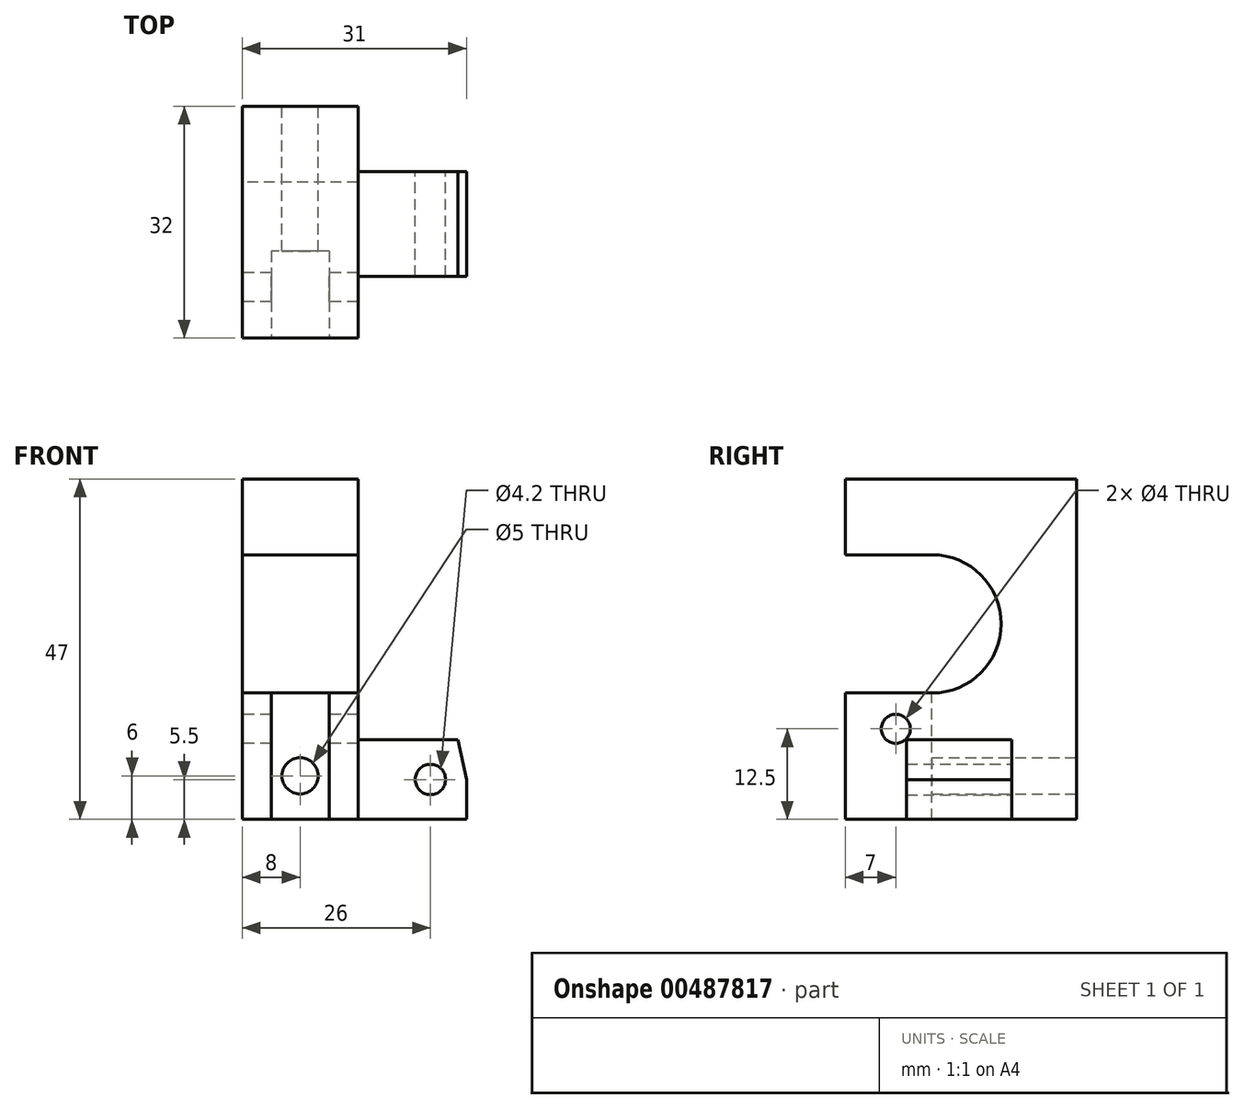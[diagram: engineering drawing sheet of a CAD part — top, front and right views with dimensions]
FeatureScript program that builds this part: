
annotation { "Feature Type Name" : "Feature", "Feature Type Description" : "" }
export const myFeature = defineFeature(function(context is Context, id is Id, definition is map)
    precondition{}
    {
        {
            var Q0;
            Q0=qCreatedBy(makeId("Right.planeOp"),FACE);
            var sketch = newSketch(context, id + "F0", { "sketchPlane" : qUnion([Q0])});
            skArc(sketch, "E0", {"start": v(0, -9.55) * mm, "mid": v(9.55, 0) * mm, "end": v(0, 9.55) * mm});
            skLineSegment(sketch, "E1.bottom", {"start": v(-12, 20) * mm, "end": v(20, 20) * mm});
            skLineSegment(sketch, "E1.top", {"start": v(-12, -27) * mm, "end": v(20, -27) * mm});
            skLineSegment(sketch, "E1.left", {"start": v(-12, 20) * mm, "end": v(-12, -27) * mm});
            skLineSegment(sketch, "E1.right", {"start": v(20, 20) * mm, "end": v(20, -27) * mm});
            skLineSegment(sketch, "E2.bottom", {"start": v(0, 9.55) * mm, "end": v(-12, 9.55) * mm});
            skLineSegment(sketch, "E2.top", {"start": v(0, -9.55) * mm, "end": v(-12, -9.55) * mm});
            skPoint(sketch, "E3.orphan", {"position": v(20, 9.55) * mm});
            skPoint(sketch, "E4.orphan", {"position": v(20, -9.55) * mm});
            skPoint(sketch, "E2.right.start.orphan", {"position": v(-20, 9.55) * mm});
            skPoint(sketch, "E5.orphan", {"position": v(-20, -9.55) * mm});
            skSolve(sketch);
        }
        {
            var Q0;
            Q0=makeQuery(id+"F0.imprint","IMPRINT",FACE,{"disambiguationData":[TD([[makeQuery(id+"F0.imprint","IMPRINT",EDGE,{"derivedFrom":sQuery(id+"F0.wireOp",EDGE,"E0")}),-1.0]])]});
            extrude(context, id + "F1", {"entities" : qUnion([Q0]), "depth" : 16 * mm, "offsetDistance" : 25 * mm});
        }
        {
            var Q0;
            Q0=makeQuery(id+"F1.opExtrude","CAP_FACE",FACE,{"disambiguationData":[OSD([sQuery(id+"F0.wireOp",EDGE,"E0"),sQuery(id+"F0.wireOp",EDGE,"E1.bottom"),sQuery(id+"F0.wireOp",EDGE,"E1.top"),sQuery(id+"F0.wireOp",EDGE,"E1.left"),sQuery(id+"F0.wireOp",EDGE,"E1.right")])],"isStart":false});
            var sketch = newSketch(context, id + "F2", { "sketchPlane" : qUnion([Q0])});
            skLineSegment(sketch, "E6.bottom", {"start": v(11, -27) * mm, "end": v(-3.5, -27) * mm});
            skLineSegment(sketch, "E6.top", {"start": v(11, -16) * mm, "end": v(-3.5, -16) * mm});
            skLineSegment(sketch, "E6.left", {"start": v(11, -27) * mm, "end": v(11, -16) * mm});
            skLineSegment(sketch, "E6.right", {"start": v(-3.5, -27) * mm, "end": v(-3.5, -16) * mm});
            skSolve(sketch);
        }
        {
            var Q0;
            Q0=makeQuery(id+"F2.imprint","IMPRINT",FACE,{"disambiguationData":[TD([[makeQuery(id+"F2.imprint","IMPRINT",EDGE,{"derivedFrom":sQuery(id+"F2.wireOp",EDGE,"E6.bottom")}),1.0]])]});
            extrude(context, id + "F3", {"entities" : qUnion([Q0]), "operationType" : NewBodyOperationType.ADD, "depth" : 15 * mm, "offsetDistance" : 25 * mm});
        }
        {
            var Q0;
            Q0=makeQuery(id+"F3.opExtrude","SWEPT_FACE",FACE,{"disambiguationData":[OSD([sQuery(id+"F2.wireOp",EDGE,"E6.right")])]});
            var sketch = newSketch(context, id + "F4", { "sketchPlane" : qUnion([Q0])});
            skLineSegment(sketch, "E7", {"start": v(31, -21.5) * mm, "end": v(31, -16) * mm});
            skLineSegment(sketch, "E8", {"start": v(31, -16) * mm, "end": v(29.83, -16) * mm});
            skLineSegment(sketch, "E9", {"start": v(29.83, -16) * mm, "end": v(31, -21.5) * mm});
            skSolve(sketch);
        }
        {
            var Q0;
            Q0=makeQuery(id+"F4.imprint","IMPRINT",FACE,{"disambiguationData":[TD([[makeQuery(id+"F4.imprint","IMPRINT",EDGE,{"derivedFrom":sQuery(id+"F4.wireOp",EDGE,"E7")}),1.0]])]});
            extrude(context, id + "F5", {"entities" : qUnion([Q0]), "operationType" : NewBodyOperationType.REMOVE, "endBound" : BoundingType.THROUGH_ALL, "oppositeDirection" : true, "depth" : 25 * mm, "offsetDistance" : 25 * mm});
        }
        {
            var Q0;
            Q0=makeQuery(id+"F3.opExtrude","SWEPT_FACE",FACE,{"disambiguationData":[OSD([sQuery(id+"F2.wireOp",EDGE,"E6.left")])]});
            var sketch = newSketch(context, id + "F6", { "sketchPlane" : qUnion([Q0])});
            skPoint(sketch, "E10", {"position": v(-26, -21.5) * mm});
            skSolve(sketch);
        }
        {
            var Q0;
            Q0=sQuery(id+"F6.wireOp",VERTEX,"E10");
            var Q1;
            Q1=makeQuery(id+"F1.opExtrude","SWEPT_BODY",BODY,{"disambiguationData":[OSD([sQuery(id+"F0.wireOp",EDGE,"E0"),sQuery(id+"F0.wireOp",EDGE,"E1.bottom"),sQuery(id+"F0.wireOp",EDGE,"E1.top"),sQuery(id+"F0.wireOp",EDGE,"E1.left"),sQuery(id+"F0.wireOp",EDGE,"E1.right"),sQuery(id+"F0.wireOp",EDGE,"E2.bottom"),sQuery(id+"F0.wireOp",EDGE,"E2.top")])]});
            hole(context, id + "F7", {"style" : HoleStyle.SIMPLE, "endStyle" : HoleEndStyle.THROUGH, "standardTappedOrClearance" : lookupTablePath({ "standard" : "ISO", "engagement" : "75%", "pitch" : "0.8 mm", "size" : "M5", "type" : "Tapped" }), "standardBlindInLast" : lookupTablePath({ "standard" : "ISO", "engagement" : "75%", "pitch" : "0.8 mm", "size" : "M5", "type" : "Tapped" }), "holeDiameter" : 4.2 * mm, "showTappedDepth" : true, "isTappedThrough" : true, "tappedDepth" : 12 * mm, "tapClearance" : 3, "locations" : qUnion([Q0]), "scope" : qUnion([Q1]), "majorDiameter" : 5 * mm});
        }
        {
            var Q0;
            Q0=makeQuery(id+"F1.opExtrude","SWEPT_FACE",FACE,{"disambiguationData":[OSD([sQuery(id+"F0.wireOp",EDGE,"E2.top")])]});
            var sketch = newSketch(context, id + "F8", { "sketchPlane" : qUnion([Q0])});
            skLineSegment(sketch, "E11.bottom", {"start": v(4, 0) * mm, "end": v(12, 0) * mm});
            skLineSegment(sketch, "E11.top", {"start": v(4, -12) * mm, "end": v(12, -12) * mm});
            skLineSegment(sketch, "E11.left", {"start": v(4, 0) * mm, "end": v(4, -12) * mm});
            skLineSegment(sketch, "E11.right", {"start": v(12, 0) * mm, "end": v(12, -12) * mm});
            skSolve(sketch);
        }
        {
            var Q0;
            Q0=makeQuery(id+"F8.imprint","IMPRINT",FACE,{"disambiguationData":[TD([[makeQuery(id+"F8.imprint","IMPRINT",EDGE,{"derivedFrom":sQuery(id+"F8.wireOp",EDGE,"E11.bottom")}),1.0]])]});
            extrude(context, id + "F9", {"entities" : qUnion([Q0]), "operationType" : NewBodyOperationType.REMOVE, "endBound" : BoundingType.THROUGH_ALL, "oppositeDirection" : true, "depth" : 25 * mm, "offsetDistance" : 25 * mm});
        }
        {
            var Q0;
            Q0=makeQuery(id+"F1.opExtrude","CAP_FACE",FACE,{"disambiguationData":[OSD([sQuery(id+"F0.wireOp",EDGE,"E0"),sQuery(id+"F0.wireOp",EDGE,"E1.bottom"),sQuery(id+"F0.wireOp",EDGE,"E1.top"),sQuery(id+"F0.wireOp",EDGE,"E1.left"),sQuery(id+"F0.wireOp",EDGE,"E1.right"),sQuery(id+"F0.wireOp",EDGE,"E2.bottom"),sQuery(id+"F0.wireOp",EDGE,"E2.top")])],"isStart":true});
            var sketch = newSketch(context, id + "F10", { "sketchPlane" : qUnion([Q0])});
            skCircle(sketch, "E12", {"center": v(5, -14.5) * mm, "radius": 2 * mm});
            skSolve(sketch);
        }
        {
            var Q0;
            Q0 = qSketchRegion(id + "F10", true);
            extrude(context, id + "F11", {"entities" : qUnion([Q0]), "operationType" : NewBodyOperationType.REMOVE, "endBound" : BoundingType.THROUGH_ALL, "oppositeDirection" : true, "depth" : 25 * mm, "offsetDistance" : 25 * mm});
        }
        {
            var Q0;
            Q0=makeQuery(id+"F1.opExtrude","SWEPT_FACE",FACE,{"disambiguationData":[OSD([sQuery(id+"F0.wireOp",EDGE,"E1.right")])]});
            var sketch = newSketch(context, id + "F12", { "sketchPlane" : qUnion([Q0])});
            skSolve(sketch);
        }
        {
            var Q0;
            {var subQ0=sQuery(id+"F0.wireOp",EDGE,"E1.right");Q0=makeQuery(id+"F12.imprint","IMPRINT",FACE,{"disambiguationData":[TD([[makeQuery(id+"F12.imprint","IMPRINT",EDGE,{"derivedFrom":makeQuery(id+"F1.opExtrude","CAP_EDGE",EDGE,{"disambiguationData":[OSD([subQ0])],"isStart":true})}),-1.0]])]});}
            var sketch = newSketch(context, id + "F13", { "sketchPlane" : qUnion([Q0])});
            skPoint(sketch, "E13", {"position": v(-8, -21) * mm});
            skSolve(sketch);
        }
        {
            var Q0;
            Q0=sQuery(id+"F13.wireOp",VERTEX,"E13");
            var Q1;
            Q1=makeQuery(id+"F1.opExtrude","SWEPT_BODY",BODY,{"disambiguationData":[OSD([sQuery(id+"F0.wireOp",EDGE,"E0"),sQuery(id+"F0.wireOp",EDGE,"E1.bottom"),sQuery(id+"F0.wireOp",EDGE,"E1.top"),sQuery(id+"F0.wireOp",EDGE,"E1.left"),sQuery(id+"F0.wireOp",EDGE,"E1.right"),sQuery(id+"F0.wireOp",EDGE,"E2.bottom"),sQuery(id+"F0.wireOp",EDGE,"E2.top")])]});
            hole(context, id + "F14", {"style" : HoleStyle.SIMPLE, "endStyle" : HoleEndStyle.THROUGH, "standardTappedOrClearance" : lookupTablePath({ "standard" : "ISO", "engagement" : "75%", "pitch" : "1 mm", "size" : "M6", "type" : "Tapped" }), "standardBlindInLast" : lookupTablePath({ "standard" : "ISO", "engagement" : "75%", "pitch" : "1 mm", "size" : "M6", "type" : "Tapped" }), "holeDiameter" : 5 * mm, "majorDiameter" : 6 * mm, "showTappedDepth" : true, "isTappedThrough" : true, "tappedDepth" : 12 * mm, "tapClearance" : 3, "locations" : qUnion([Q0]), "scope" : qUnion([Q1])});
        }
    });
